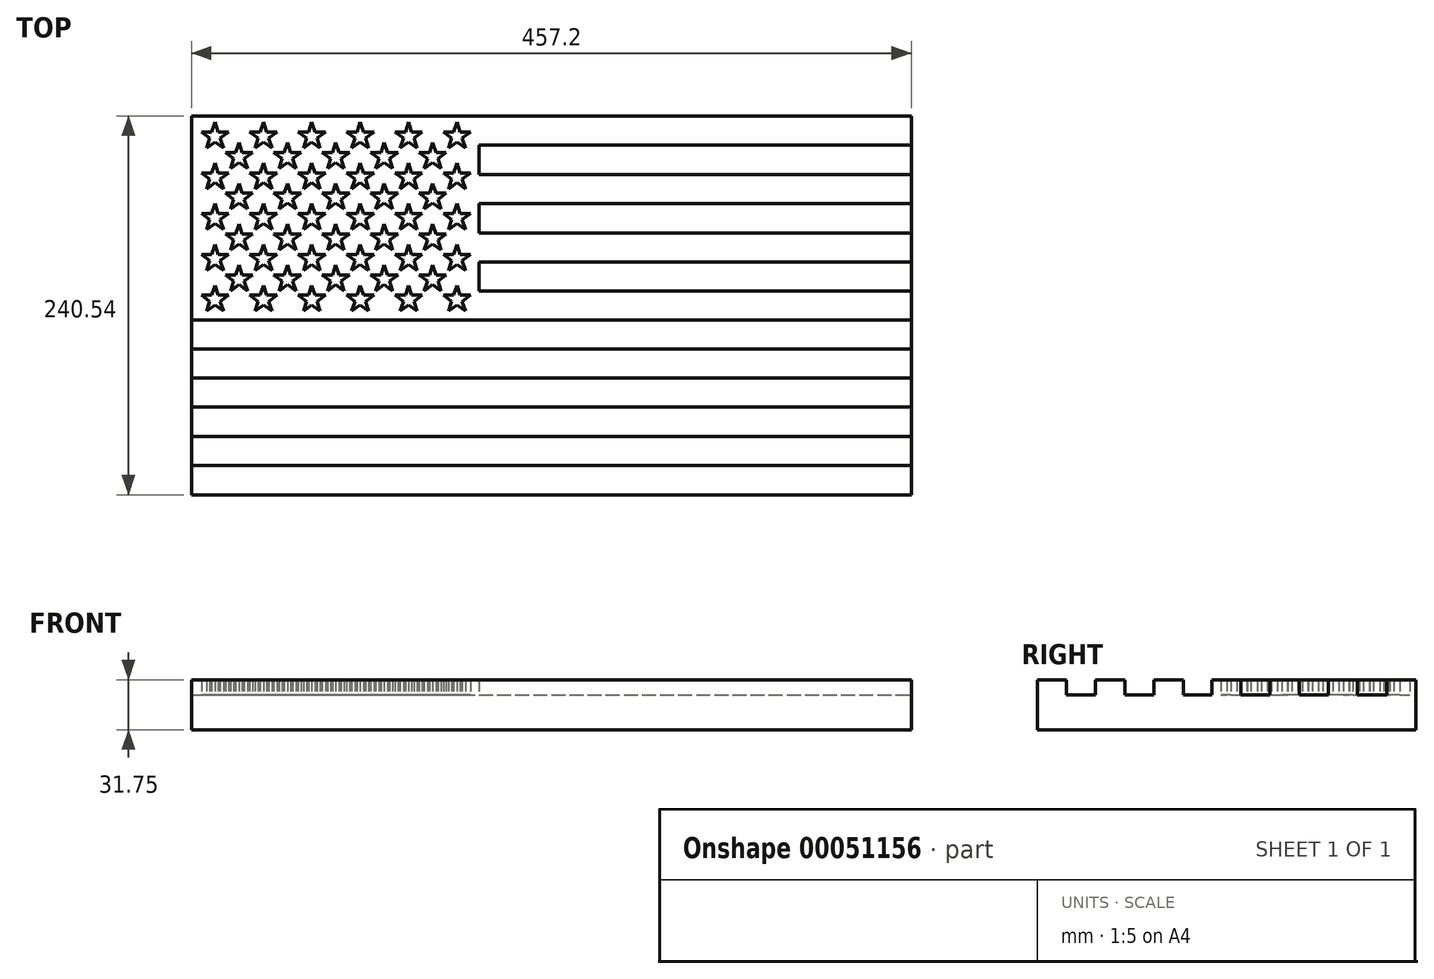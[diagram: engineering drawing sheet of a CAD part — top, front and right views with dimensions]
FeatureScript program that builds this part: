
annotation { "Feature Type Name" : "Feature", "Feature Type Description" : "" }
export const myFeature = defineFeature(function(context is Context, id is Id, definition is map)
    precondition{}
    {
        {
            var Q0;
            Q0=qCreatedBy(makeId("Top.planeOp"),FACE);
            var sketch = newSketch(context, id + "F0", { "sketchPlane" : qUnion([Q0])});
            skLineSegment(sketch, "E0.rect.bottom", {"start": v(228.6, 120.27) * mm, "end": v(-228.6, 120.27) * mm});
            skLineSegment(sketch, "E0.rect.top", {"start": v(228.6, -120.27) * mm, "end": v(-228.6, -120.27) * mm});
            skLineSegment(sketch, "E0.rect.left", {"start": v(228.6, 120.27) * mm, "end": v(228.6, -120.27) * mm});
            skLineSegment(sketch, "E0.rect.right", {"start": v(-228.6, 120.27) * mm, "end": v(-228.6, -120.27) * mm});
            skPoint(sketch, "E0.rect.middle", {"position": v(0, 0) * mm});
            skSolve(sketch);
        }
        {
            var Q0;
            Q0 = qSketchRegion(id + "F0", true);
            extrude(context, id + "F1", {"entities" : qUnion([Q0]), "depth" : 22.22 * mm});
        }
        {
            var Q0;
            Q0=makeQuery(id+"F1.opExtrude","CAP_FACE",FACE,{"disambiguationData":[OSD([sQuery(id+"F0.wireOp",EDGE,"E0.rect.bottom"),sQuery(id+"F0.wireOp",EDGE,"E0.rect.top"),sQuery(id+"F0.wireOp",EDGE,"E0.rect.left"),sQuery(id+"F0.wireOp",EDGE,"E0.rect.right")])],"isStart":false});
            var sketch = newSketch(context, id + "F2", { "sketchPlane" : qUnion([Q0])});
            skLineSegment(sketch, "E1.bottom", {"start": v(-228.6, 120.27) * mm, "end": v(-45.97, 120.27) * mm});
            skLineSegment(sketch, "E1.top", {"start": v(-228.6, -9.25) * mm, "end": v(-45.97, -9.25) * mm});
            skLineSegment(sketch, "E1.left", {"start": v(-228.6, 120.27) * mm, "end": v(-228.6, -9.25) * mm});
            skLineSegment(sketch, "E1.right", {"start": v(-45.97, 120.27) * mm, "end": v(-45.97, -9.25) * mm});
            skLineSegment(sketch, "E2.bottom", {"start": v(-45.97, 120.27) * mm, "end": v(228.6, 120.27) * mm});
            skLineSegment(sketch, "E2.top", {"start": v(-45.97, 101.73) * mm, "end": v(228.6, 101.73) * mm});
            skLineSegment(sketch, "E2.left", {"start": v(-45.97, 120.27) * mm, "end": v(-45.97, 101.73) * mm});
            skLineSegment(sketch, "E2.right", {"start": v(228.6, 120.27) * mm, "end": v(228.6, 101.73) * mm});
            skLineSegment(sketch, "E3.MirrorCS", {"start": v(-45.97, 83.19) * mm, "end": v(228.6, 83.19) * mm});
            skLineSegment(sketch, "E4.MirrorCS", {"start": v(-45.97, 64.64) * mm, "end": v(228.6, 64.64) * mm});
            skLineSegment(sketch, "E5.MirrorCS", {"start": v(-45.97, 46.1) * mm, "end": v(228.6, 46.1) * mm});
            skLineSegment(sketch, "E6.MirrorCS", {"start": v(-45.97, 27.56) * mm, "end": v(228.6, 27.56) * mm});
            skLineSegment(sketch, "E7.MirrorCS", {"start": v(-45.97, 9.02) * mm, "end": v(228.6, 9.02) * mm});
            skLineSegment(sketch, "E8", {"start": v(-45.97, -9.25) * mm, "end": v(228.6, -9.25) * mm});
            skLineSegment(sketch, "E9.bottom", {"start": v(-228.6, -120.27) * mm, "end": v(228.6, -120.27) * mm});
            skLineSegment(sketch, "E9.top", {"start": v(-228.6, -101.73) * mm, "end": v(228.6, -101.73) * mm});
            skLineSegment(sketch, "E9.left", {"start": v(-228.6, -120.27) * mm, "end": v(-228.6, -101.73) * mm});
            skLineSegment(sketch, "E9.right", {"start": v(228.6, -120.27) * mm, "end": v(228.6, -101.73) * mm});
            skLineSegment(sketch, "E10.MirrorCS", {"start": v(-228.6, -83.19) * mm, "end": v(228.6, -83.19) * mm});
            skLineSegment(sketch, "E11.MirrorCS", {"start": v(-228.6, -64.64) * mm, "end": v(228.6, -64.64) * mm});
            skLineSegment(sketch, "E12.MirrorCS", {"start": v(-228.6, -46.1) * mm, "end": v(228.6, -46.1) * mm});
            skLineSegment(sketch, "E13.MirrorCS", {"start": v(-228.6, -27.56) * mm, "end": v(228.6, -27.56) * mm});
            skLineSegment(sketch, "E14.bottom", {"start": v(-228.6, 120.27) * mm, "end": v(-213.61, 120.27) * mm});
            skLineSegment(sketch, "E14.left", {"start": v(-228.6, 120.27) * mm, "end": v(-228.6, 107.31) * mm});
            skLineSegment(sketch, "E15.trimOffspring", {"start": v(-210.03, 108.18) * mm, "end": v(-210.03, 108.18) * mm});
            skLineSegment(sketch, "E16", {"start": v(-222.27, 110.13) * mm, "end": v(-215.66, 110.13) * mm});
            skLineSegment(sketch, "E17", {"start": v(-204.95, 110.13) * mm, "end": v(-210.3, 106.24) * mm});
            skLineSegment(sketch, "E18", {"start": v(-218.97, 99.95) * mm, "end": v(-216.92, 106.24) * mm});
            skLineSegment(sketch, "E19", {"start": v(-213.61, 116.42) * mm, "end": v(-211.57, 110.13) * mm});
            skLineSegment(sketch, "E20", {"start": v(-208.26, 99.95) * mm, "end": v(-213.61, 103.84) * mm});
            skLineSegment(sketch, "E21.trimOffspring", {"start": v(-210.3, 106.24) * mm, "end": v(-208.26, 99.95) * mm});
            skLineSegment(sketch, "E22.trimOffspring", {"start": v(-211.57, 110.13) * mm, "end": v(-204.95, 110.13) * mm});
            skLineSegment(sketch, "E23.trimOffspring", {"start": v(-215.66, 110.13) * mm, "end": v(-213.61, 116.42) * mm});
            skLineSegment(sketch, "E24.trimOffspring", {"start": v(-216.92, 106.24) * mm, "end": v(-222.27, 110.13) * mm});
            skLineSegment(sketch, "E25.trimOffspring", {"start": v(-213.61, 103.84) * mm, "end": v(-218.97, 99.95) * mm});
            skLineSegment(sketch, "E26.0.1.0", {"start": v(-218.97, 74.04) * mm, "end": v(-216.92, 80.33) * mm});
            skLineSegment(sketch, "E26.0.1.1", {"start": v(-210.3, 80.33) * mm, "end": v(-208.26, 74.04) * mm});
            skLineSegment(sketch, "E26.0.1.2", {"start": v(-211.57, 84.22) * mm, "end": v(-204.95, 84.22) * mm});
            skLineSegment(sketch, "E26.0.1.3", {"start": v(-216.92, 80.33) * mm, "end": v(-222.27, 84.22) * mm});
            skLineSegment(sketch, "E26.0.1.4", {"start": v(-213.61, 77.93) * mm, "end": v(-218.97, 74.04) * mm});
            skLineSegment(sketch, "E26.0.1.5", {"start": v(-213.61, 90.51) * mm, "end": v(-211.57, 84.22) * mm});
            skLineSegment(sketch, "E26.0.1.6", {"start": v(-215.66, 84.22) * mm, "end": v(-213.61, 90.51) * mm});
            skLineSegment(sketch, "E26.0.1.7", {"start": v(-222.27, 84.22) * mm, "end": v(-215.66, 84.22) * mm});
            skLineSegment(sketch, "E26.0.1.8", {"start": v(-208.26, 74.04) * mm, "end": v(-213.61, 77.93) * mm});
            skLineSegment(sketch, "E26.0.1.9", {"start": v(-204.95, 84.22) * mm, "end": v(-210.3, 80.33) * mm});
            skLineSegment(sketch, "E26.0.2.0", {"start": v(-218.97, 48.13) * mm, "end": v(-216.92, 54.42) * mm});
            skLineSegment(sketch, "E26.0.2.1", {"start": v(-210.3, 54.42) * mm, "end": v(-208.26, 48.13) * mm});
            skLineSegment(sketch, "E26.0.2.2", {"start": v(-211.57, 58.31) * mm, "end": v(-204.95, 58.31) * mm});
            skLineSegment(sketch, "E26.0.2.3", {"start": v(-216.92, 54.42) * mm, "end": v(-222.27, 58.31) * mm});
            skLineSegment(sketch, "E26.0.2.4", {"start": v(-213.61, 52.02) * mm, "end": v(-218.97, 48.13) * mm});
            skLineSegment(sketch, "E26.0.2.5", {"start": v(-213.61, 64.6) * mm, "end": v(-211.57, 58.31) * mm});
            skLineSegment(sketch, "E26.0.2.6", {"start": v(-215.66, 58.31) * mm, "end": v(-213.61, 64.6) * mm});
            skLineSegment(sketch, "E26.0.2.7", {"start": v(-222.27, 58.31) * mm, "end": v(-215.66, 58.31) * mm});
            skLineSegment(sketch, "E26.0.2.8", {"start": v(-208.26, 48.13) * mm, "end": v(-213.61, 52.02) * mm});
            skLineSegment(sketch, "E26.0.2.9", {"start": v(-204.95, 58.31) * mm, "end": v(-210.3, 54.42) * mm});
            skLineSegment(sketch, "E26.0.3.0", {"start": v(-218.97, 22.23) * mm, "end": v(-216.92, 28.52) * mm});
            skLineSegment(sketch, "E26.0.3.1", {"start": v(-210.3, 28.52) * mm, "end": v(-208.26, 22.23) * mm});
            skLineSegment(sketch, "E26.0.3.2", {"start": v(-211.57, 32.4) * mm, "end": v(-204.95, 32.4) * mm});
            skLineSegment(sketch, "E26.0.3.3", {"start": v(-216.92, 28.52) * mm, "end": v(-222.27, 32.4) * mm});
            skLineSegment(sketch, "E26.0.3.4", {"start": v(-213.61, 26.11) * mm, "end": v(-218.97, 22.23) * mm});
            skLineSegment(sketch, "E26.0.3.5", {"start": v(-213.61, 38.7) * mm, "end": v(-211.57, 32.4) * mm});
            skLineSegment(sketch, "E26.0.3.6", {"start": v(-215.66, 32.4) * mm, "end": v(-213.61, 38.7) * mm});
            skLineSegment(sketch, "E26.0.3.7", {"start": v(-222.27, 32.4) * mm, "end": v(-215.66, 32.4) * mm});
            skLineSegment(sketch, "E26.0.3.8", {"start": v(-208.26, 22.23) * mm, "end": v(-213.61, 26.11) * mm});
            skLineSegment(sketch, "E26.0.3.9", {"start": v(-204.95, 32.4) * mm, "end": v(-210.3, 28.52) * mm});
            skLineSegment(sketch, "E26.0.4.0", {"start": v(-218.97, -3.68) * mm, "end": v(-216.92, 2.6) * mm});
            skLineSegment(sketch, "E26.0.4.1", {"start": v(-210.3, 2.6) * mm, "end": v(-208.26, -3.68) * mm});
            skLineSegment(sketch, "E26.0.4.2", {"start": v(-211.57, 6.5) * mm, "end": v(-204.95, 6.5) * mm});
            skLineSegment(sketch, "E26.0.4.3", {"start": v(-216.92, 2.6) * mm, "end": v(-222.27, 6.5) * mm});
            skLineSegment(sketch, "E26.0.4.4", {"start": v(-213.61, 0.2) * mm, "end": v(-218.97, -3.68) * mm});
            skLineSegment(sketch, "E26.0.4.5", {"start": v(-213.61, 12.79) * mm, "end": v(-211.57, 6.5) * mm});
            skLineSegment(sketch, "E26.0.4.6", {"start": v(-215.66, 6.5) * mm, "end": v(-213.61, 12.79) * mm});
            skLineSegment(sketch, "E26.0.4.7", {"start": v(-222.27, 6.5) * mm, "end": v(-215.66, 6.5) * mm});
            skLineSegment(sketch, "E26.0.4.8", {"start": v(-208.26, -3.68) * mm, "end": v(-213.61, 0.2) * mm});
            skLineSegment(sketch, "E26.0.4.9", {"start": v(-204.95, 6.5) * mm, "end": v(-210.3, 2.6) * mm});
            skLineSegment(sketch, "E26.1.0.0", {"start": v(-188.23, 99.95) * mm, "end": v(-186.19, 106.24) * mm});
            skLineSegment(sketch, "E26.1.0.1", {"start": v(-179.57, 106.24) * mm, "end": v(-177.53, 99.95) * mm});
            skLineSegment(sketch, "E26.1.0.2", {"start": v(-180.84, 110.13) * mm, "end": v(-174.22, 110.13) * mm});
            skLineSegment(sketch, "E26.1.0.3", {"start": v(-186.19, 106.24) * mm, "end": v(-191.54, 110.13) * mm});
            skLineSegment(sketch, "E26.1.0.4", {"start": v(-182.88, 103.84) * mm, "end": v(-188.23, 99.95) * mm});
            skLineSegment(sketch, "E26.1.0.5", {"start": v(-182.88, 116.42) * mm, "end": v(-180.84, 110.13) * mm});
            skLineSegment(sketch, "E26.1.0.6", {"start": v(-184.92, 110.13) * mm, "end": v(-182.88, 116.42) * mm});
            skLineSegment(sketch, "E26.1.0.7", {"start": v(-191.54, 110.13) * mm, "end": v(-184.92, 110.13) * mm});
            skLineSegment(sketch, "E26.1.0.8", {"start": v(-177.53, 99.95) * mm, "end": v(-182.88, 103.84) * mm});
            skLineSegment(sketch, "E26.1.0.9", {"start": v(-174.22, 110.13) * mm, "end": v(-179.57, 106.24) * mm});
            skLineSegment(sketch, "E26.1.1.0", {"start": v(-188.23, 74.04) * mm, "end": v(-186.19, 80.33) * mm});
            skLineSegment(sketch, "E26.1.1.1", {"start": v(-179.57, 80.33) * mm, "end": v(-177.53, 74.04) * mm});
            skLineSegment(sketch, "E26.1.1.2", {"start": v(-180.84, 84.22) * mm, "end": v(-174.22, 84.22) * mm});
            skLineSegment(sketch, "E26.1.1.3", {"start": v(-186.19, 80.33) * mm, "end": v(-191.54, 84.22) * mm});
            skLineSegment(sketch, "E26.1.1.4", {"start": v(-182.88, 77.93) * mm, "end": v(-188.23, 74.04) * mm});
            skLineSegment(sketch, "E26.1.1.5", {"start": v(-182.88, 90.51) * mm, "end": v(-180.84, 84.22) * mm});
            skLineSegment(sketch, "E26.1.1.6", {"start": v(-184.92, 84.22) * mm, "end": v(-182.88, 90.51) * mm});
            skLineSegment(sketch, "E26.1.1.7", {"start": v(-191.54, 84.22) * mm, "end": v(-184.92, 84.22) * mm});
            skLineSegment(sketch, "E26.1.1.8", {"start": v(-177.53, 74.04) * mm, "end": v(-182.88, 77.93) * mm});
            skLineSegment(sketch, "E26.1.1.9", {"start": v(-174.22, 84.22) * mm, "end": v(-179.57, 80.33) * mm});
            skLineSegment(sketch, "E26.1.2.0", {"start": v(-188.23, 48.13) * mm, "end": v(-186.19, 54.42) * mm});
            skLineSegment(sketch, "E26.1.2.1", {"start": v(-179.57, 54.42) * mm, "end": v(-177.53, 48.13) * mm});
            skLineSegment(sketch, "E26.1.2.2", {"start": v(-180.84, 58.31) * mm, "end": v(-174.22, 58.31) * mm});
            skLineSegment(sketch, "E26.1.2.3", {"start": v(-186.19, 54.42) * mm, "end": v(-191.54, 58.31) * mm});
            skLineSegment(sketch, "E26.1.2.4", {"start": v(-182.88, 52.02) * mm, "end": v(-188.23, 48.13) * mm});
            skLineSegment(sketch, "E26.1.2.5", {"start": v(-182.88, 64.6) * mm, "end": v(-180.84, 58.31) * mm});
            skLineSegment(sketch, "E26.1.2.6", {"start": v(-184.92, 58.31) * mm, "end": v(-182.88, 64.6) * mm});
            skLineSegment(sketch, "E26.1.2.7", {"start": v(-191.54, 58.31) * mm, "end": v(-184.92, 58.31) * mm});
            skLineSegment(sketch, "E26.1.2.8", {"start": v(-177.53, 48.13) * mm, "end": v(-182.88, 52.02) * mm});
            skLineSegment(sketch, "E26.1.2.9", {"start": v(-174.22, 58.31) * mm, "end": v(-179.57, 54.42) * mm});
            skLineSegment(sketch, "E26.1.3.0", {"start": v(-188.23, 22.23) * mm, "end": v(-186.19, 28.52) * mm});
            skLineSegment(sketch, "E26.1.3.1", {"start": v(-179.57, 28.52) * mm, "end": v(-177.53, 22.23) * mm});
            skLineSegment(sketch, "E26.1.3.2", {"start": v(-180.84, 32.4) * mm, "end": v(-174.22, 32.4) * mm});
            skLineSegment(sketch, "E26.1.3.3", {"start": v(-186.19, 28.52) * mm, "end": v(-191.54, 32.4) * mm});
            skLineSegment(sketch, "E26.1.3.4", {"start": v(-182.88, 26.11) * mm, "end": v(-188.23, 22.23) * mm});
            skLineSegment(sketch, "E26.1.3.5", {"start": v(-182.88, 38.7) * mm, "end": v(-180.84, 32.4) * mm});
            skLineSegment(sketch, "E26.1.3.6", {"start": v(-184.92, 32.4) * mm, "end": v(-182.88, 38.7) * mm});
            skLineSegment(sketch, "E26.1.3.7", {"start": v(-191.54, 32.4) * mm, "end": v(-184.92, 32.4) * mm});
            skLineSegment(sketch, "E26.1.3.8", {"start": v(-177.53, 22.23) * mm, "end": v(-182.88, 26.11) * mm});
            skLineSegment(sketch, "E26.1.3.9", {"start": v(-174.22, 32.4) * mm, "end": v(-179.57, 28.52) * mm});
            skLineSegment(sketch, "E26.1.4.0", {"start": v(-188.23, -3.68) * mm, "end": v(-186.19, 2.6) * mm});
            skLineSegment(sketch, "E26.1.4.1", {"start": v(-179.57, 2.6) * mm, "end": v(-177.53, -3.68) * mm});
            skLineSegment(sketch, "E26.1.4.2", {"start": v(-180.84, 6.5) * mm, "end": v(-174.22, 6.5) * mm});
            skLineSegment(sketch, "E26.1.4.3", {"start": v(-186.19, 2.6) * mm, "end": v(-191.54, 6.5) * mm});
            skLineSegment(sketch, "E26.1.4.4", {"start": v(-182.88, 0.2) * mm, "end": v(-188.23, -3.68) * mm});
            skLineSegment(sketch, "E26.1.4.5", {"start": v(-182.88, 12.79) * mm, "end": v(-180.84, 6.5) * mm});
            skLineSegment(sketch, "E26.1.4.6", {"start": v(-184.92, 6.5) * mm, "end": v(-182.88, 12.79) * mm});
            skLineSegment(sketch, "E26.1.4.7", {"start": v(-191.54, 6.5) * mm, "end": v(-184.92, 6.5) * mm});
            skLineSegment(sketch, "E26.1.4.8", {"start": v(-177.53, -3.68) * mm, "end": v(-182.88, 0.2) * mm});
            skLineSegment(sketch, "E26.1.4.9", {"start": v(-174.22, 6.5) * mm, "end": v(-179.57, 2.6) * mm});
            skLineSegment(sketch, "E26.2.0.0", {"start": v(-157.5, 99.95) * mm, "end": v(-155.45, 106.24) * mm});
            skLineSegment(sketch, "E26.2.0.1", {"start": v(-148.84, 106.24) * mm, "end": v(-146.8, 99.95) * mm});
            skLineSegment(sketch, "E26.2.0.2", {"start": v(-150.1, 110.13) * mm, "end": v(-143.49, 110.13) * mm});
            skLineSegment(sketch, "E26.2.0.3", {"start": v(-155.45, 106.24) * mm, "end": v(-160.8, 110.13) * mm});
            skLineSegment(sketch, "E26.2.0.4", {"start": v(-152.15, 103.84) * mm, "end": v(-157.5, 99.95) * mm});
            skLineSegment(sketch, "E26.2.0.5", {"start": v(-152.15, 116.42) * mm, "end": v(-150.1, 110.13) * mm});
            skLineSegment(sketch, "E26.2.0.6", {"start": v(-154.2, 110.13) * mm, "end": v(-152.15, 116.42) * mm});
            skLineSegment(sketch, "E26.2.0.7", {"start": v(-160.8, 110.13) * mm, "end": v(-154.2, 110.13) * mm});
            skLineSegment(sketch, "E26.2.0.8", {"start": v(-146.8, 99.95) * mm, "end": v(-152.15, 103.84) * mm});
            skLineSegment(sketch, "E26.2.0.9", {"start": v(-143.49, 110.13) * mm, "end": v(-148.84, 106.24) * mm});
            skLineSegment(sketch, "E26.2.1.0", {"start": v(-157.5, 74.04) * mm, "end": v(-155.45, 80.33) * mm});
            skLineSegment(sketch, "E26.2.1.1", {"start": v(-148.84, 80.33) * mm, "end": v(-146.8, 74.04) * mm});
            skLineSegment(sketch, "E26.2.1.2", {"start": v(-150.1, 84.22) * mm, "end": v(-143.49, 84.22) * mm});
            skLineSegment(sketch, "E26.2.1.3", {"start": v(-155.45, 80.33) * mm, "end": v(-160.8, 84.22) * mm});
            skLineSegment(sketch, "E26.2.1.4", {"start": v(-152.15, 77.93) * mm, "end": v(-157.5, 74.04) * mm});
            skLineSegment(sketch, "E26.2.1.5", {"start": v(-152.15, 90.51) * mm, "end": v(-150.1, 84.22) * mm});
            skLineSegment(sketch, "E26.2.1.6", {"start": v(-154.2, 84.22) * mm, "end": v(-152.15, 90.51) * mm});
            skLineSegment(sketch, "E26.2.1.7", {"start": v(-160.8, 84.22) * mm, "end": v(-154.2, 84.22) * mm});
            skLineSegment(sketch, "E26.2.1.8", {"start": v(-146.8, 74.04) * mm, "end": v(-152.15, 77.93) * mm});
            skLineSegment(sketch, "E26.2.1.9", {"start": v(-143.49, 84.22) * mm, "end": v(-148.84, 80.33) * mm});
            skLineSegment(sketch, "E26.2.2.0", {"start": v(-157.5, 48.13) * mm, "end": v(-155.45, 54.42) * mm});
            skLineSegment(sketch, "E26.2.2.1", {"start": v(-148.84, 54.42) * mm, "end": v(-146.8, 48.13) * mm});
            skLineSegment(sketch, "E26.2.2.2", {"start": v(-150.1, 58.31) * mm, "end": v(-143.49, 58.31) * mm});
            skLineSegment(sketch, "E26.2.2.3", {"start": v(-155.45, 54.42) * mm, "end": v(-160.8, 58.31) * mm});
            skLineSegment(sketch, "E26.2.2.4", {"start": v(-152.15, 52.02) * mm, "end": v(-157.5, 48.13) * mm});
            skLineSegment(sketch, "E26.2.2.5", {"start": v(-152.15, 64.6) * mm, "end": v(-150.1, 58.31) * mm});
            skLineSegment(sketch, "E26.2.2.6", {"start": v(-154.2, 58.31) * mm, "end": v(-152.15, 64.6) * mm});
            skLineSegment(sketch, "E26.2.2.7", {"start": v(-160.8, 58.31) * mm, "end": v(-154.2, 58.31) * mm});
            skLineSegment(sketch, "E26.2.2.8", {"start": v(-146.8, 48.13) * mm, "end": v(-152.15, 52.02) * mm});
            skLineSegment(sketch, "E26.2.2.9", {"start": v(-143.49, 58.31) * mm, "end": v(-148.84, 54.42) * mm});
            skLineSegment(sketch, "E26.2.3.0", {"start": v(-157.5, 22.23) * mm, "end": v(-155.45, 28.52) * mm});
            skLineSegment(sketch, "E26.2.3.1", {"start": v(-148.84, 28.52) * mm, "end": v(-146.8, 22.23) * mm});
            skLineSegment(sketch, "E26.2.3.2", {"start": v(-150.1, 32.4) * mm, "end": v(-143.49, 32.4) * mm});
            skLineSegment(sketch, "E26.2.3.3", {"start": v(-155.45, 28.52) * mm, "end": v(-160.8, 32.4) * mm});
            skLineSegment(sketch, "E26.2.3.4", {"start": v(-152.15, 26.11) * mm, "end": v(-157.5, 22.23) * mm});
            skLineSegment(sketch, "E26.2.3.5", {"start": v(-152.15, 38.7) * mm, "end": v(-150.1, 32.4) * mm});
            skLineSegment(sketch, "E26.2.3.6", {"start": v(-154.2, 32.4) * mm, "end": v(-152.15, 38.7) * mm});
            skLineSegment(sketch, "E26.2.3.7", {"start": v(-160.8, 32.4) * mm, "end": v(-154.2, 32.4) * mm});
            skLineSegment(sketch, "E26.2.3.8", {"start": v(-146.8, 22.23) * mm, "end": v(-152.15, 26.11) * mm});
            skLineSegment(sketch, "E26.2.3.9", {"start": v(-143.49, 32.4) * mm, "end": v(-148.84, 28.52) * mm});
            skLineSegment(sketch, "E26.2.4.0", {"start": v(-157.5, -3.68) * mm, "end": v(-155.45, 2.6) * mm});
            skLineSegment(sketch, "E26.2.4.1", {"start": v(-148.84, 2.6) * mm, "end": v(-146.8, -3.68) * mm});
            skLineSegment(sketch, "E26.2.4.2", {"start": v(-150.1, 6.5) * mm, "end": v(-143.49, 6.5) * mm});
            skLineSegment(sketch, "E26.2.4.3", {"start": v(-155.45, 2.6) * mm, "end": v(-160.8, 6.5) * mm});
            skLineSegment(sketch, "E26.2.4.4", {"start": v(-152.15, 0.2) * mm, "end": v(-157.5, -3.68) * mm});
            skLineSegment(sketch, "E26.2.4.5", {"start": v(-152.15, 12.79) * mm, "end": v(-150.1, 6.5) * mm});
            skLineSegment(sketch, "E26.2.4.6", {"start": v(-154.2, 6.5) * mm, "end": v(-152.15, 12.79) * mm});
            skLineSegment(sketch, "E26.2.4.7", {"start": v(-160.8, 6.5) * mm, "end": v(-154.2, 6.5) * mm});
            skLineSegment(sketch, "E26.2.4.8", {"start": v(-146.8, -3.68) * mm, "end": v(-152.15, 0.2) * mm});
            skLineSegment(sketch, "E26.2.4.9", {"start": v(-143.49, 6.5) * mm, "end": v(-148.84, 2.6) * mm});
            skLineSegment(sketch, "E26.3.0.0", {"start": v(-126.76, 99.95) * mm, "end": v(-124.72, 106.24) * mm});
            skLineSegment(sketch, "E26.3.0.1", {"start": v(-118.1, 106.24) * mm, "end": v(-116.06, 99.95) * mm});
            skLineSegment(sketch, "E26.3.0.2", {"start": v(-119.37, 110.13) * mm, "end": v(-112.75, 110.13) * mm});
            skLineSegment(sketch, "E26.3.0.3", {"start": v(-124.72, 106.24) * mm, "end": v(-130.07, 110.13) * mm});
            skLineSegment(sketch, "E26.3.0.4", {"start": v(-121.41, 103.84) * mm, "end": v(-126.76, 99.95) * mm});
            skLineSegment(sketch, "E26.3.0.5", {"start": v(-121.41, 116.42) * mm, "end": v(-119.37, 110.13) * mm});
            skLineSegment(sketch, "E26.3.0.6", {"start": v(-123.46, 110.13) * mm, "end": v(-121.41, 116.42) * mm});
            skLineSegment(sketch, "E26.3.0.7", {"start": v(-130.07, 110.13) * mm, "end": v(-123.46, 110.13) * mm});
            skLineSegment(sketch, "E26.3.0.8", {"start": v(-116.06, 99.95) * mm, "end": v(-121.41, 103.84) * mm});
            skLineSegment(sketch, "E26.3.0.9", {"start": v(-112.75, 110.13) * mm, "end": v(-118.1, 106.24) * mm});
            skLineSegment(sketch, "E26.3.1.0", {"start": v(-126.76, 74.04) * mm, "end": v(-124.72, 80.33) * mm});
            skLineSegment(sketch, "E26.3.1.1", {"start": v(-118.1, 80.33) * mm, "end": v(-116.06, 74.04) * mm});
            skLineSegment(sketch, "E26.3.1.2", {"start": v(-119.37, 84.22) * mm, "end": v(-112.75, 84.22) * mm});
            skLineSegment(sketch, "E26.3.1.3", {"start": v(-124.72, 80.33) * mm, "end": v(-130.07, 84.22) * mm});
            skLineSegment(sketch, "E26.3.1.4", {"start": v(-121.41, 77.93) * mm, "end": v(-126.76, 74.04) * mm});
            skLineSegment(sketch, "E26.3.1.5", {"start": v(-121.41, 90.51) * mm, "end": v(-119.37, 84.22) * mm});
            skLineSegment(sketch, "E26.3.1.6", {"start": v(-123.46, 84.22) * mm, "end": v(-121.41, 90.51) * mm});
            skLineSegment(sketch, "E26.3.1.7", {"start": v(-130.07, 84.22) * mm, "end": v(-123.46, 84.22) * mm});
            skLineSegment(sketch, "E26.3.1.8", {"start": v(-116.06, 74.04) * mm, "end": v(-121.41, 77.93) * mm});
            skLineSegment(sketch, "E26.3.1.9", {"start": v(-112.75, 84.22) * mm, "end": v(-118.1, 80.33) * mm});
            skLineSegment(sketch, "E26.3.2.0", {"start": v(-126.76, 48.13) * mm, "end": v(-124.72, 54.42) * mm});
            skLineSegment(sketch, "E26.3.2.1", {"start": v(-118.1, 54.42) * mm, "end": v(-116.06, 48.13) * mm});
            skLineSegment(sketch, "E26.3.2.2", {"start": v(-119.37, 58.31) * mm, "end": v(-112.75, 58.31) * mm});
            skLineSegment(sketch, "E26.3.2.3", {"start": v(-124.72, 54.42) * mm, "end": v(-130.07, 58.31) * mm});
            skLineSegment(sketch, "E26.3.2.4", {"start": v(-121.41, 52.02) * mm, "end": v(-126.76, 48.13) * mm});
            skLineSegment(sketch, "E26.3.2.5", {"start": v(-121.41, 64.6) * mm, "end": v(-119.37, 58.31) * mm});
            skLineSegment(sketch, "E26.3.2.6", {"start": v(-123.46, 58.31) * mm, "end": v(-121.41, 64.6) * mm});
            skLineSegment(sketch, "E26.3.2.7", {"start": v(-130.07, 58.31) * mm, "end": v(-123.46, 58.31) * mm});
            skLineSegment(sketch, "E26.3.2.8", {"start": v(-116.06, 48.13) * mm, "end": v(-121.41, 52.02) * mm});
            skLineSegment(sketch, "E26.3.2.9", {"start": v(-112.75, 58.31) * mm, "end": v(-118.1, 54.42) * mm});
            skLineSegment(sketch, "E26.3.3.0", {"start": v(-126.76, 22.23) * mm, "end": v(-124.72, 28.52) * mm});
            skLineSegment(sketch, "E26.3.3.1", {"start": v(-118.1, 28.52) * mm, "end": v(-116.06, 22.23) * mm});
            skLineSegment(sketch, "E26.3.3.2", {"start": v(-119.37, 32.4) * mm, "end": v(-112.75, 32.4) * mm});
            skLineSegment(sketch, "E26.3.3.3", {"start": v(-124.72, 28.52) * mm, "end": v(-130.07, 32.4) * mm});
            skLineSegment(sketch, "E26.3.3.4", {"start": v(-121.41, 26.11) * mm, "end": v(-126.76, 22.23) * mm});
            skLineSegment(sketch, "E26.3.3.5", {"start": v(-121.41, 38.7) * mm, "end": v(-119.37, 32.4) * mm});
            skLineSegment(sketch, "E26.3.3.6", {"start": v(-123.46, 32.4) * mm, "end": v(-121.41, 38.7) * mm});
            skLineSegment(sketch, "E26.3.3.7", {"start": v(-130.07, 32.4) * mm, "end": v(-123.46, 32.4) * mm});
            skLineSegment(sketch, "E26.3.3.8", {"start": v(-116.06, 22.23) * mm, "end": v(-121.41, 26.11) * mm});
            skLineSegment(sketch, "E26.3.3.9", {"start": v(-112.75, 32.4) * mm, "end": v(-118.1, 28.52) * mm});
            skLineSegment(sketch, "E26.3.4.0", {"start": v(-126.76, -3.68) * mm, "end": v(-124.72, 2.6) * mm});
            skLineSegment(sketch, "E26.3.4.1", {"start": v(-118.1, 2.6) * mm, "end": v(-116.06, -3.68) * mm});
            skLineSegment(sketch, "E26.3.4.2", {"start": v(-119.37, 6.5) * mm, "end": v(-112.75, 6.5) * mm});
            skLineSegment(sketch, "E26.3.4.3", {"start": v(-124.72, 2.6) * mm, "end": v(-130.07, 6.5) * mm});
            skLineSegment(sketch, "E26.3.4.4", {"start": v(-121.41, 0.2) * mm, "end": v(-126.76, -3.68) * mm});
            skLineSegment(sketch, "E26.3.4.5", {"start": v(-121.41, 12.79) * mm, "end": v(-119.37, 6.5) * mm});
            skLineSegment(sketch, "E26.3.4.6", {"start": v(-123.46, 6.5) * mm, "end": v(-121.41, 12.79) * mm});
            skLineSegment(sketch, "E26.3.4.7", {"start": v(-130.07, 6.5) * mm, "end": v(-123.46, 6.5) * mm});
            skLineSegment(sketch, "E26.3.4.8", {"start": v(-116.06, -3.68) * mm, "end": v(-121.41, 0.2) * mm});
            skLineSegment(sketch, "E26.3.4.9", {"start": v(-112.75, 6.5) * mm, "end": v(-118.1, 2.6) * mm});
            skLineSegment(sketch, "E26.4.0.0", {"start": v(-96.03, 99.95) * mm, "end": v(-93.99, 106.24) * mm});
            skLineSegment(sketch, "E26.4.0.1", {"start": v(-87.37, 106.24) * mm, "end": v(-85.33, 99.95) * mm});
            skLineSegment(sketch, "E26.4.0.2", {"start": v(-88.63, 110.13) * mm, "end": v(-82.02, 110.13) * mm});
            skLineSegment(sketch, "E26.4.0.3", {"start": v(-93.99, 106.24) * mm, "end": v(-99.34, 110.13) * mm});
            skLineSegment(sketch, "E26.4.0.4", {"start": v(-90.68, 103.84) * mm, "end": v(-96.03, 99.95) * mm});
            skLineSegment(sketch, "E26.4.0.5", {"start": v(-90.68, 116.42) * mm, "end": v(-88.63, 110.13) * mm});
            skLineSegment(sketch, "E26.4.0.6", {"start": v(-92.72, 110.13) * mm, "end": v(-90.68, 116.42) * mm});
            skLineSegment(sketch, "E26.4.0.7", {"start": v(-99.34, 110.13) * mm, "end": v(-92.72, 110.13) * mm});
            skLineSegment(sketch, "E26.4.0.8", {"start": v(-85.33, 99.95) * mm, "end": v(-90.68, 103.84) * mm});
            skLineSegment(sketch, "E26.4.0.9", {"start": v(-82.02, 110.13) * mm, "end": v(-87.37, 106.24) * mm});
            skLineSegment(sketch, "E26.4.1.0", {"start": v(-96.03, 74.04) * mm, "end": v(-93.99, 80.33) * mm});
            skLineSegment(sketch, "E26.4.1.1", {"start": v(-87.37, 80.33) * mm, "end": v(-85.33, 74.04) * mm});
            skLineSegment(sketch, "E26.4.1.2", {"start": v(-88.63, 84.22) * mm, "end": v(-82.02, 84.22) * mm});
            skLineSegment(sketch, "E26.4.1.3", {"start": v(-93.99, 80.33) * mm, "end": v(-99.34, 84.22) * mm});
            skLineSegment(sketch, "E26.4.1.4", {"start": v(-90.68, 77.93) * mm, "end": v(-96.03, 74.04) * mm});
            skLineSegment(sketch, "E26.4.1.5", {"start": v(-90.68, 90.51) * mm, "end": v(-88.63, 84.22) * mm});
            skLineSegment(sketch, "E26.4.1.6", {"start": v(-92.72, 84.22) * mm, "end": v(-90.68, 90.51) * mm});
            skLineSegment(sketch, "E26.4.1.7", {"start": v(-99.34, 84.22) * mm, "end": v(-92.72, 84.22) * mm});
            skLineSegment(sketch, "E26.4.1.8", {"start": v(-85.33, 74.04) * mm, "end": v(-90.68, 77.93) * mm});
            skLineSegment(sketch, "E26.4.1.9", {"start": v(-82.02, 84.22) * mm, "end": v(-87.37, 80.33) * mm});
            skLineSegment(sketch, "E26.4.2.0", {"start": v(-96.03, 48.13) * mm, "end": v(-93.99, 54.42) * mm});
            skLineSegment(sketch, "E26.4.2.1", {"start": v(-87.37, 54.42) * mm, "end": v(-85.33, 48.13) * mm});
            skLineSegment(sketch, "E26.4.2.2", {"start": v(-88.63, 58.31) * mm, "end": v(-82.02, 58.31) * mm});
            skLineSegment(sketch, "E26.4.2.3", {"start": v(-93.99, 54.42) * mm, "end": v(-99.34, 58.31) * mm});
            skLineSegment(sketch, "E26.4.2.4", {"start": v(-90.68, 52.02) * mm, "end": v(-96.03, 48.13) * mm});
            skLineSegment(sketch, "E26.4.2.5", {"start": v(-90.68, 64.6) * mm, "end": v(-88.63, 58.31) * mm});
            skLineSegment(sketch, "E26.4.2.6", {"start": v(-92.72, 58.31) * mm, "end": v(-90.68, 64.6) * mm});
            skLineSegment(sketch, "E26.4.2.7", {"start": v(-99.34, 58.31) * mm, "end": v(-92.72, 58.31) * mm});
            skLineSegment(sketch, "E26.4.2.8", {"start": v(-85.33, 48.13) * mm, "end": v(-90.68, 52.02) * mm});
            skLineSegment(sketch, "E26.4.2.9", {"start": v(-82.02, 58.31) * mm, "end": v(-87.37, 54.42) * mm});
            skLineSegment(sketch, "E26.4.3.0", {"start": v(-96.03, 22.23) * mm, "end": v(-93.99, 28.52) * mm});
            skLineSegment(sketch, "E26.4.3.1", {"start": v(-87.37, 28.52) * mm, "end": v(-85.33, 22.23) * mm});
            skLineSegment(sketch, "E26.4.3.2", {"start": v(-88.63, 32.4) * mm, "end": v(-82.02, 32.4) * mm});
            skLineSegment(sketch, "E26.4.3.3", {"start": v(-93.99, 28.52) * mm, "end": v(-99.34, 32.4) * mm});
            skLineSegment(sketch, "E26.4.3.4", {"start": v(-90.68, 26.11) * mm, "end": v(-96.03, 22.23) * mm});
            skLineSegment(sketch, "E26.4.3.5", {"start": v(-90.68, 38.7) * mm, "end": v(-88.63, 32.4) * mm});
            skLineSegment(sketch, "E26.4.3.6", {"start": v(-92.72, 32.4) * mm, "end": v(-90.68, 38.7) * mm});
            skLineSegment(sketch, "E26.4.3.7", {"start": v(-99.34, 32.4) * mm, "end": v(-92.72, 32.4) * mm});
            skLineSegment(sketch, "E26.4.3.8", {"start": v(-85.33, 22.23) * mm, "end": v(-90.68, 26.11) * mm});
            skLineSegment(sketch, "E26.4.3.9", {"start": v(-82.02, 32.4) * mm, "end": v(-87.37, 28.52) * mm});
            skLineSegment(sketch, "E26.4.4.0", {"start": v(-96.03, -3.68) * mm, "end": v(-93.99, 2.6) * mm});
            skLineSegment(sketch, "E26.4.4.1", {"start": v(-87.37, 2.6) * mm, "end": v(-85.33, -3.68) * mm});
            skLineSegment(sketch, "E26.4.4.2", {"start": v(-88.63, 6.5) * mm, "end": v(-82.02, 6.5) * mm});
            skLineSegment(sketch, "E26.4.4.3", {"start": v(-93.99, 2.6) * mm, "end": v(-99.34, 6.5) * mm});
            skLineSegment(sketch, "E26.4.4.4", {"start": v(-90.68, 0.2) * mm, "end": v(-96.03, -3.68) * mm});
            skLineSegment(sketch, "E26.4.4.5", {"start": v(-90.68, 12.79) * mm, "end": v(-88.63, 6.5) * mm});
            skLineSegment(sketch, "E26.4.4.6", {"start": v(-92.72, 6.5) * mm, "end": v(-90.68, 12.79) * mm});
            skLineSegment(sketch, "E26.4.4.7", {"start": v(-99.34, 6.5) * mm, "end": v(-92.72, 6.5) * mm});
            skLineSegment(sketch, "E26.4.4.8", {"start": v(-85.33, -3.68) * mm, "end": v(-90.68, 0.2) * mm});
            skLineSegment(sketch, "E26.4.4.9", {"start": v(-82.02, 6.5) * mm, "end": v(-87.37, 2.6) * mm});
            skLineSegment(sketch, "E26.5.0.0", {"start": v(-65.3, 99.95) * mm, "end": v(-63.25, 106.24) * mm});
            skLineSegment(sketch, "E26.5.0.1", {"start": v(-56.64, 106.24) * mm, "end": v(-54.6, 99.95) * mm});
            skLineSegment(sketch, "E26.5.0.2", {"start": v(-57.9, 110.13) * mm, "end": v(-51.28, 110.13) * mm});
            skLineSegment(sketch, "E26.5.0.3", {"start": v(-63.25, 106.24) * mm, "end": v(-68.6, 110.13) * mm});
            skLineSegment(sketch, "E26.5.0.4", {"start": v(-59.94, 103.84) * mm, "end": v(-65.3, 99.95) * mm});
            skLineSegment(sketch, "E26.5.0.5", {"start": v(-59.94, 116.42) * mm, "end": v(-57.9, 110.13) * mm});
            skLineSegment(sketch, "E26.5.0.6", {"start": v(-61.99, 110.13) * mm, "end": v(-59.94, 116.42) * mm});
            skLineSegment(sketch, "E26.5.0.7", {"start": v(-68.6, 110.13) * mm, "end": v(-61.99, 110.13) * mm});
            skLineSegment(sketch, "E26.5.0.8", {"start": v(-54.6, 99.95) * mm, "end": v(-59.94, 103.84) * mm});
            skLineSegment(sketch, "E26.5.0.9", {"start": v(-51.28, 110.13) * mm, "end": v(-56.64, 106.24) * mm});
            skLineSegment(sketch, "E26.5.1.0", {"start": v(-65.3, 74.04) * mm, "end": v(-63.25, 80.33) * mm});
            skLineSegment(sketch, "E26.5.1.1", {"start": v(-56.64, 80.33) * mm, "end": v(-54.6, 74.04) * mm});
            skLineSegment(sketch, "E26.5.1.2", {"start": v(-57.9, 84.22) * mm, "end": v(-51.28, 84.22) * mm});
            skLineSegment(sketch, "E26.5.1.3", {"start": v(-63.25, 80.33) * mm, "end": v(-68.6, 84.22) * mm});
            skLineSegment(sketch, "E26.5.1.4", {"start": v(-59.94, 77.93) * mm, "end": v(-65.3, 74.04) * mm});
            skLineSegment(sketch, "E26.5.1.5", {"start": v(-59.94, 90.51) * mm, "end": v(-57.9, 84.22) * mm});
            skLineSegment(sketch, "E26.5.1.6", {"start": v(-61.99, 84.22) * mm, "end": v(-59.94, 90.51) * mm});
            skLineSegment(sketch, "E26.5.1.7", {"start": v(-68.6, 84.22) * mm, "end": v(-61.99, 84.22) * mm});
            skLineSegment(sketch, "E26.5.1.8", {"start": v(-54.6, 74.04) * mm, "end": v(-59.94, 77.93) * mm});
            skLineSegment(sketch, "E26.5.1.9", {"start": v(-51.28, 84.22) * mm, "end": v(-56.64, 80.33) * mm});
            skLineSegment(sketch, "E26.5.2.0", {"start": v(-65.3, 48.13) * mm, "end": v(-63.25, 54.42) * mm});
            skLineSegment(sketch, "E26.5.2.1", {"start": v(-56.64, 54.42) * mm, "end": v(-54.6, 48.13) * mm});
            skLineSegment(sketch, "E26.5.2.2", {"start": v(-57.9, 58.31) * mm, "end": v(-51.28, 58.31) * mm});
            skLineSegment(sketch, "E26.5.2.3", {"start": v(-63.25, 54.42) * mm, "end": v(-68.6, 58.31) * mm});
            skLineSegment(sketch, "E26.5.2.4", {"start": v(-59.94, 52.02) * mm, "end": v(-65.3, 48.13) * mm});
            skLineSegment(sketch, "E26.5.2.5", {"start": v(-59.94, 64.6) * mm, "end": v(-57.9, 58.31) * mm});
            skLineSegment(sketch, "E26.5.2.6", {"start": v(-61.99, 58.31) * mm, "end": v(-59.94, 64.6) * mm});
            skLineSegment(sketch, "E26.5.2.7", {"start": v(-68.6, 58.31) * mm, "end": v(-61.99, 58.31) * mm});
            skLineSegment(sketch, "E26.5.2.8", {"start": v(-54.6, 48.13) * mm, "end": v(-59.94, 52.02) * mm});
            skLineSegment(sketch, "E26.5.2.9", {"start": v(-51.28, 58.31) * mm, "end": v(-56.64, 54.42) * mm});
            skLineSegment(sketch, "E26.5.3.0", {"start": v(-65.3, 22.23) * mm, "end": v(-63.25, 28.52) * mm});
            skLineSegment(sketch, "E26.5.3.1", {"start": v(-56.64, 28.52) * mm, "end": v(-54.6, 22.23) * mm});
            skLineSegment(sketch, "E26.5.3.2", {"start": v(-57.9, 32.4) * mm, "end": v(-51.28, 32.4) * mm});
            skLineSegment(sketch, "E26.5.3.3", {"start": v(-63.25, 28.52) * mm, "end": v(-68.6, 32.4) * mm});
            skLineSegment(sketch, "E26.5.3.4", {"start": v(-59.94, 26.11) * mm, "end": v(-65.3, 22.23) * mm});
            skLineSegment(sketch, "E26.5.3.5", {"start": v(-59.94, 38.7) * mm, "end": v(-57.9, 32.4) * mm});
            skLineSegment(sketch, "E26.5.3.6", {"start": v(-61.99, 32.4) * mm, "end": v(-59.94, 38.7) * mm});
            skLineSegment(sketch, "E26.5.3.7", {"start": v(-68.6, 32.4) * mm, "end": v(-61.99, 32.4) * mm});
            skLineSegment(sketch, "E26.5.3.8", {"start": v(-54.6, 22.23) * mm, "end": v(-59.94, 26.11) * mm});
            skLineSegment(sketch, "E26.5.3.9", {"start": v(-51.28, 32.4) * mm, "end": v(-56.64, 28.52) * mm});
            skLineSegment(sketch, "E26.5.4.0", {"start": v(-65.3, -3.68) * mm, "end": v(-63.25, 2.6) * mm});
            skLineSegment(sketch, "E26.5.4.1", {"start": v(-56.64, 2.6) * mm, "end": v(-54.6, -3.68) * mm});
            skLineSegment(sketch, "E26.5.4.2", {"start": v(-57.9, 6.5) * mm, "end": v(-51.28, 6.5) * mm});
            skLineSegment(sketch, "E26.5.4.3", {"start": v(-63.25, 2.6) * mm, "end": v(-68.6, 6.5) * mm});
            skLineSegment(sketch, "E26.5.4.4", {"start": v(-59.94, 0.2) * mm, "end": v(-65.3, -3.68) * mm});
            skLineSegment(sketch, "E26.5.4.5", {"start": v(-59.94, 12.79) * mm, "end": v(-57.9, 6.5) * mm});
            skLineSegment(sketch, "E26.5.4.6", {"start": v(-61.99, 6.5) * mm, "end": v(-59.94, 12.79) * mm});
            skLineSegment(sketch, "E26.5.4.7", {"start": v(-68.6, 6.5) * mm, "end": v(-61.99, 6.5) * mm});
            skLineSegment(sketch, "E26.5.4.8", {"start": v(-54.6, -3.68) * mm, "end": v(-59.94, 0.2) * mm});
            skLineSegment(sketch, "E26.5.4.9", {"start": v(-51.28, 6.5) * mm, "end": v(-56.64, 2.6) * mm});
            skLineSegment(sketch, "E26.direction1", {"start": v(-218.97, 99.95) * mm, "end": v(-188.23, 99.95) * mm, "construction": true});
            skLineSegment(sketch, "E26.direction2", {"start": v(-218.97, 99.95) * mm, "end": v(-218.97, 74.04) * mm, "construction": true});
            skLineSegment(sketch, "E27.bottom", {"start": v(-228.6, 120.27) * mm, "end": v(-198.37, 120.27) * mm});
            skLineSegment(sketch, "E27.left", {"start": v(-228.6, 120.27) * mm, "end": v(-228.6, 94.36) * mm});
            skLineSegment(sketch, "E28", {"start": v(-198.37, 103.47) * mm, "end": v(-200.42, 97.17) * mm});
            skLineSegment(sketch, "E29", {"start": v(-203.73, 87) * mm, "end": v(-198.37, 90.88) * mm});
            skLineSegment(sketch, "E30", {"start": v(-189.71, 97.17) * mm, "end": v(-196.33, 97.17) * mm});
            skLineSegment(sketch, "E31", {"start": v(-207.03, 97.17) * mm, "end": v(-201.68, 93.29) * mm});
            skLineSegment(sketch, "E32", {"start": v(-193.02, 87) * mm, "end": v(-195.07, 93.29) * mm});
            skLineSegment(sketch, "E33.trimOffspring", {"start": v(-196.33, 97.17) * mm, "end": v(-198.37, 103.47) * mm});
            skLineSegment(sketch, "E34.trimOffspring", {"start": v(-200.42, 97.17) * mm, "end": v(-207.03, 97.17) * mm});
            skLineSegment(sketch, "E35.trimOffspring", {"start": v(-201.68, 93.29) * mm, "end": v(-203.73, 87) * mm});
            skLineSegment(sketch, "E36.trimOffspring", {"start": v(-198.37, 90.88) * mm, "end": v(-193.02, 87) * mm});
            skLineSegment(sketch, "E37.trimOffspring", {"start": v(-195.07, 93.29) * mm, "end": v(-189.71, 97.17) * mm});
            skLineSegment(sketch, "E38.0.1.0", {"start": v(-198.37, 64.98) * mm, "end": v(-193.02, 61.09) * mm});
            skLineSegment(sketch, "E38.0.1.1", {"start": v(-195.07, 67.38) * mm, "end": v(-189.71, 71.27) * mm});
            skLineSegment(sketch, "E38.0.1.2", {"start": v(-193.02, 61.09) * mm, "end": v(-195.07, 67.38) * mm});
            skLineSegment(sketch, "E38.0.1.3", {"start": v(-201.68, 67.38) * mm, "end": v(-203.73, 61.09) * mm});
            skLineSegment(sketch, "E38.0.1.4", {"start": v(-189.71, 71.27) * mm, "end": v(-196.33, 71.27) * mm});
            skLineSegment(sketch, "E38.0.1.5", {"start": v(-203.73, 61.09) * mm, "end": v(-198.37, 64.98) * mm});
            skLineSegment(sketch, "E38.0.1.6", {"start": v(-200.42, 71.27) * mm, "end": v(-207.03, 71.27) * mm});
            skLineSegment(sketch, "E38.0.1.7", {"start": v(-207.03, 71.27) * mm, "end": v(-201.68, 67.38) * mm});
            skLineSegment(sketch, "E38.0.1.8", {"start": v(-198.37, 77.56) * mm, "end": v(-200.42, 71.27) * mm});
            skLineSegment(sketch, "E38.0.1.9", {"start": v(-196.33, 71.27) * mm, "end": v(-198.37, 77.56) * mm});
            skLineSegment(sketch, "E38.0.2.0", {"start": v(-198.37, 39.07) * mm, "end": v(-193.02, 35.18) * mm});
            skLineSegment(sketch, "E38.0.2.1", {"start": v(-195.07, 41.47) * mm, "end": v(-189.71, 45.36) * mm});
            skLineSegment(sketch, "E38.0.2.2", {"start": v(-193.02, 35.18) * mm, "end": v(-195.07, 41.47) * mm});
            skLineSegment(sketch, "E38.0.2.3", {"start": v(-201.68, 41.47) * mm, "end": v(-203.73, 35.18) * mm});
            skLineSegment(sketch, "E38.0.2.4", {"start": v(-189.71, 45.36) * mm, "end": v(-196.33, 45.36) * mm});
            skLineSegment(sketch, "E38.0.2.5", {"start": v(-203.73, 35.18) * mm, "end": v(-198.37, 39.07) * mm});
            skLineSegment(sketch, "E38.0.2.6", {"start": v(-200.42, 45.36) * mm, "end": v(-207.03, 45.36) * mm});
            skLineSegment(sketch, "E38.0.2.7", {"start": v(-207.03, 45.36) * mm, "end": v(-201.68, 41.47) * mm});
            skLineSegment(sketch, "E38.0.2.8", {"start": v(-198.37, 51.65) * mm, "end": v(-200.42, 45.36) * mm});
            skLineSegment(sketch, "E38.0.2.9", {"start": v(-196.33, 45.36) * mm, "end": v(-198.37, 51.65) * mm});
            skLineSegment(sketch, "E38.0.3.0", {"start": v(-198.37, 13.16) * mm, "end": v(-193.02, 9.27) * mm});
            skLineSegment(sketch, "E38.0.3.1", {"start": v(-195.07, 15.56) * mm, "end": v(-189.71, 19.45) * mm});
            skLineSegment(sketch, "E38.0.3.2", {"start": v(-193.02, 9.27) * mm, "end": v(-195.07, 15.56) * mm});
            skLineSegment(sketch, "E38.0.3.3", {"start": v(-201.68, 15.56) * mm, "end": v(-203.73, 9.27) * mm});
            skLineSegment(sketch, "E38.0.3.4", {"start": v(-189.71, 19.45) * mm, "end": v(-196.33, 19.45) * mm});
            skLineSegment(sketch, "E38.0.3.5", {"start": v(-203.73, 9.27) * mm, "end": v(-198.37, 13.16) * mm});
            skLineSegment(sketch, "E38.0.3.6", {"start": v(-200.42, 19.45) * mm, "end": v(-207.03, 19.45) * mm});
            skLineSegment(sketch, "E38.0.3.7", {"start": v(-207.03, 19.45) * mm, "end": v(-201.68, 15.56) * mm});
            skLineSegment(sketch, "E38.0.3.8", {"start": v(-198.37, 25.74) * mm, "end": v(-200.42, 19.45) * mm});
            skLineSegment(sketch, "E38.0.3.9", {"start": v(-196.33, 19.45) * mm, "end": v(-198.37, 25.74) * mm});
            skLineSegment(sketch, "E38.1.0.0", {"start": v(-167.64, 90.88) * mm, "end": v(-162.29, 87) * mm});
            skLineSegment(sketch, "E38.1.0.1", {"start": v(-164.33, 93.29) * mm, "end": v(-158.98, 97.17) * mm});
            skLineSegment(sketch, "E38.1.0.2", {"start": v(-162.29, 87) * mm, "end": v(-164.33, 93.29) * mm});
            skLineSegment(sketch, "E38.1.0.3", {"start": v(-170.95, 93.29) * mm, "end": v(-173, 87) * mm});
            skLineSegment(sketch, "E38.1.0.4", {"start": v(-158.98, 97.17) * mm, "end": v(-165.6, 97.17) * mm});
            skLineSegment(sketch, "E38.1.0.5", {"start": v(-173, 87) * mm, "end": v(-167.64, 90.88) * mm});
            skLineSegment(sketch, "E38.1.0.6", {"start": v(-169.68, 97.17) * mm, "end": v(-176.3, 97.17) * mm});
            skLineSegment(sketch, "E38.1.0.7", {"start": v(-176.3, 97.17) * mm, "end": v(-170.95, 93.29) * mm});
            skLineSegment(sketch, "E38.1.0.8", {"start": v(-167.64, 103.47) * mm, "end": v(-169.68, 97.17) * mm});
            skLineSegment(sketch, "E38.1.0.9", {"start": v(-165.6, 97.17) * mm, "end": v(-167.64, 103.47) * mm});
            skLineSegment(sketch, "E38.1.1.0", {"start": v(-167.64, 64.98) * mm, "end": v(-162.29, 61.09) * mm});
            skLineSegment(sketch, "E38.1.1.1", {"start": v(-164.33, 67.38) * mm, "end": v(-158.98, 71.27) * mm});
            skLineSegment(sketch, "E38.1.1.2", {"start": v(-162.29, 61.09) * mm, "end": v(-164.33, 67.38) * mm});
            skLineSegment(sketch, "E38.1.1.3", {"start": v(-170.95, 67.38) * mm, "end": v(-173, 61.09) * mm});
            skLineSegment(sketch, "E38.1.1.4", {"start": v(-158.98, 71.27) * mm, "end": v(-165.6, 71.27) * mm});
            skLineSegment(sketch, "E38.1.1.5", {"start": v(-173, 61.09) * mm, "end": v(-167.64, 64.98) * mm});
            skLineSegment(sketch, "E38.1.1.6", {"start": v(-169.68, 71.27) * mm, "end": v(-176.3, 71.27) * mm});
            skLineSegment(sketch, "E38.1.1.7", {"start": v(-176.3, 71.27) * mm, "end": v(-170.95, 67.38) * mm});
            skLineSegment(sketch, "E38.1.1.8", {"start": v(-167.64, 77.56) * mm, "end": v(-169.68, 71.27) * mm});
            skLineSegment(sketch, "E38.1.1.9", {"start": v(-165.6, 71.27) * mm, "end": v(-167.64, 77.56) * mm});
            skLineSegment(sketch, "E38.1.2.0", {"start": v(-167.64, 39.07) * mm, "end": v(-162.29, 35.18) * mm});
            skLineSegment(sketch, "E38.1.2.1", {"start": v(-164.33, 41.47) * mm, "end": v(-158.98, 45.36) * mm});
            skLineSegment(sketch, "E38.1.2.2", {"start": v(-162.29, 35.18) * mm, "end": v(-164.33, 41.47) * mm});
            skLineSegment(sketch, "E38.1.2.3", {"start": v(-170.95, 41.47) * mm, "end": v(-173, 35.18) * mm});
            skLineSegment(sketch, "E38.1.2.4", {"start": v(-158.98, 45.36) * mm, "end": v(-165.6, 45.36) * mm});
            skLineSegment(sketch, "E38.1.2.5", {"start": v(-173, 35.18) * mm, "end": v(-167.64, 39.07) * mm});
            skLineSegment(sketch, "E38.1.2.6", {"start": v(-169.68, 45.36) * mm, "end": v(-176.3, 45.36) * mm});
            skLineSegment(sketch, "E38.1.2.7", {"start": v(-176.3, 45.36) * mm, "end": v(-170.95, 41.47) * mm});
            skLineSegment(sketch, "E38.1.2.8", {"start": v(-167.64, 51.65) * mm, "end": v(-169.68, 45.36) * mm});
            skLineSegment(sketch, "E38.1.2.9", {"start": v(-165.6, 45.36) * mm, "end": v(-167.64, 51.65) * mm});
            skLineSegment(sketch, "E38.1.3.0", {"start": v(-167.64, 13.16) * mm, "end": v(-162.29, 9.27) * mm});
            skLineSegment(sketch, "E38.1.3.1", {"start": v(-164.33, 15.56) * mm, "end": v(-158.98, 19.45) * mm});
            skLineSegment(sketch, "E38.1.3.2", {"start": v(-162.29, 9.27) * mm, "end": v(-164.33, 15.56) * mm});
            skLineSegment(sketch, "E38.1.3.3", {"start": v(-170.95, 15.56) * mm, "end": v(-173, 9.27) * mm});
            skLineSegment(sketch, "E38.1.3.4", {"start": v(-158.98, 19.45) * mm, "end": v(-165.6, 19.45) * mm});
            skLineSegment(sketch, "E38.1.3.5", {"start": v(-173, 9.27) * mm, "end": v(-167.64, 13.16) * mm});
            skLineSegment(sketch, "E38.1.3.6", {"start": v(-169.68, 19.45) * mm, "end": v(-176.3, 19.45) * mm});
            skLineSegment(sketch, "E38.1.3.7", {"start": v(-176.3, 19.45) * mm, "end": v(-170.95, 15.56) * mm});
            skLineSegment(sketch, "E38.1.3.8", {"start": v(-167.64, 25.74) * mm, "end": v(-169.68, 19.45) * mm});
            skLineSegment(sketch, "E38.1.3.9", {"start": v(-165.6, 19.45) * mm, "end": v(-167.64, 25.74) * mm});
            skLineSegment(sketch, "E38.2.0.0", {"start": v(-136.9, 90.88) * mm, "end": v(-131.55, 87) * mm});
            skLineSegment(sketch, "E38.2.0.1", {"start": v(-133.6, 93.29) * mm, "end": v(-128.25, 97.17) * mm});
            skLineSegment(sketch, "E38.2.0.2", {"start": v(-131.55, 87) * mm, "end": v(-133.6, 93.29) * mm});
            skLineSegment(sketch, "E38.2.0.3", {"start": v(-140.21, 93.29) * mm, "end": v(-142.26, 87) * mm});
            skLineSegment(sketch, "E38.2.0.4", {"start": v(-128.25, 97.17) * mm, "end": v(-134.86, 97.17) * mm});
            skLineSegment(sketch, "E38.2.0.5", {"start": v(-142.26, 87) * mm, "end": v(-136.9, 90.88) * mm});
            skLineSegment(sketch, "E38.2.0.6", {"start": v(-138.95, 97.17) * mm, "end": v(-145.57, 97.17) * mm});
            skLineSegment(sketch, "E38.2.0.7", {"start": v(-145.57, 97.17) * mm, "end": v(-140.21, 93.29) * mm});
            skLineSegment(sketch, "E38.2.0.8", {"start": v(-136.9, 103.47) * mm, "end": v(-138.95, 97.17) * mm});
            skLineSegment(sketch, "E38.2.0.9", {"start": v(-134.86, 97.17) * mm, "end": v(-136.9, 103.47) * mm});
            skLineSegment(sketch, "E38.2.1.0", {"start": v(-136.9, 64.98) * mm, "end": v(-131.55, 61.09) * mm});
            skLineSegment(sketch, "E38.2.1.1", {"start": v(-133.6, 67.38) * mm, "end": v(-128.25, 71.27) * mm});
            skLineSegment(sketch, "E38.2.1.2", {"start": v(-131.55, 61.09) * mm, "end": v(-133.6, 67.38) * mm});
            skLineSegment(sketch, "E38.2.1.3", {"start": v(-140.21, 67.38) * mm, "end": v(-142.26, 61.09) * mm});
            skLineSegment(sketch, "E38.2.1.4", {"start": v(-128.25, 71.27) * mm, "end": v(-134.86, 71.27) * mm});
            skLineSegment(sketch, "E38.2.1.5", {"start": v(-142.26, 61.09) * mm, "end": v(-136.9, 64.98) * mm});
            skLineSegment(sketch, "E38.2.1.6", {"start": v(-138.95, 71.27) * mm, "end": v(-145.57, 71.27) * mm});
            skLineSegment(sketch, "E38.2.1.7", {"start": v(-145.57, 71.27) * mm, "end": v(-140.21, 67.38) * mm});
            skLineSegment(sketch, "E38.2.1.8", {"start": v(-136.9, 77.56) * mm, "end": v(-138.95, 71.27) * mm});
            skLineSegment(sketch, "E38.2.1.9", {"start": v(-134.86, 71.27) * mm, "end": v(-136.9, 77.56) * mm});
            skLineSegment(sketch, "E38.2.2.0", {"start": v(-136.9, 39.07) * mm, "end": v(-131.55, 35.18) * mm});
            skLineSegment(sketch, "E38.2.2.1", {"start": v(-133.6, 41.47) * mm, "end": v(-128.25, 45.36) * mm});
            skLineSegment(sketch, "E38.2.2.2", {"start": v(-131.55, 35.18) * mm, "end": v(-133.6, 41.47) * mm});
            skLineSegment(sketch, "E38.2.2.3", {"start": v(-140.21, 41.47) * mm, "end": v(-142.26, 35.18) * mm});
            skLineSegment(sketch, "E38.2.2.4", {"start": v(-128.25, 45.36) * mm, "end": v(-134.86, 45.36) * mm});
            skLineSegment(sketch, "E38.2.2.5", {"start": v(-142.26, 35.18) * mm, "end": v(-136.9, 39.07) * mm});
            skLineSegment(sketch, "E38.2.2.6", {"start": v(-138.95, 45.36) * mm, "end": v(-145.57, 45.36) * mm});
            skLineSegment(sketch, "E38.2.2.7", {"start": v(-145.57, 45.36) * mm, "end": v(-140.21, 41.47) * mm});
            skLineSegment(sketch, "E38.2.2.8", {"start": v(-136.9, 51.65) * mm, "end": v(-138.95, 45.36) * mm});
            skLineSegment(sketch, "E38.2.2.9", {"start": v(-134.86, 45.36) * mm, "end": v(-136.9, 51.65) * mm});
            skLineSegment(sketch, "E38.2.3.0", {"start": v(-136.9, 13.16) * mm, "end": v(-131.55, 9.27) * mm});
            skLineSegment(sketch, "E38.2.3.1", {"start": v(-133.6, 15.56) * mm, "end": v(-128.25, 19.45) * mm});
            skLineSegment(sketch, "E38.2.3.2", {"start": v(-131.55, 9.27) * mm, "end": v(-133.6, 15.56) * mm});
            skLineSegment(sketch, "E38.2.3.3", {"start": v(-140.21, 15.56) * mm, "end": v(-142.26, 9.27) * mm});
            skLineSegment(sketch, "E38.2.3.4", {"start": v(-128.25, 19.45) * mm, "end": v(-134.86, 19.45) * mm});
            skLineSegment(sketch, "E38.2.3.5", {"start": v(-142.26, 9.27) * mm, "end": v(-136.9, 13.16) * mm});
            skLineSegment(sketch, "E38.2.3.6", {"start": v(-138.95, 19.45) * mm, "end": v(-145.57, 19.45) * mm});
            skLineSegment(sketch, "E38.2.3.7", {"start": v(-145.57, 19.45) * mm, "end": v(-140.21, 15.56) * mm});
            skLineSegment(sketch, "E38.2.3.8", {"start": v(-136.9, 25.74) * mm, "end": v(-138.95, 19.45) * mm});
            skLineSegment(sketch, "E38.2.3.9", {"start": v(-134.86, 19.45) * mm, "end": v(-136.9, 25.74) * mm});
            skLineSegment(sketch, "E38.3.0.0", {"start": v(-106.17, 90.88) * mm, "end": v(-100.82, 87) * mm});
            skLineSegment(sketch, "E38.3.0.1", {"start": v(-102.86, 93.29) * mm, "end": v(-97.51, 97.17) * mm});
            skLineSegment(sketch, "E38.3.0.2", {"start": v(-100.82, 87) * mm, "end": v(-102.86, 93.29) * mm});
            skLineSegment(sketch, "E38.3.0.3", {"start": v(-109.48, 93.29) * mm, "end": v(-111.52, 87) * mm});
            skLineSegment(sketch, "E38.3.0.4", {"start": v(-97.51, 97.17) * mm, "end": v(-104.13, 97.17) * mm});
            skLineSegment(sketch, "E38.3.0.5", {"start": v(-111.52, 87) * mm, "end": v(-106.17, 90.88) * mm});
            skLineSegment(sketch, "E38.3.0.6", {"start": v(-108.22, 97.17) * mm, "end": v(-114.83, 97.17) * mm});
            skLineSegment(sketch, "E38.3.0.7", {"start": v(-114.83, 97.17) * mm, "end": v(-109.48, 93.29) * mm});
            skLineSegment(sketch, "E38.3.0.8", {"start": v(-106.17, 103.47) * mm, "end": v(-108.22, 97.17) * mm});
            skLineSegment(sketch, "E38.3.0.9", {"start": v(-104.13, 97.17) * mm, "end": v(-106.17, 103.47) * mm});
            skLineSegment(sketch, "E38.3.1.0", {"start": v(-106.17, 64.98) * mm, "end": v(-100.82, 61.09) * mm});
            skLineSegment(sketch, "E38.3.1.1", {"start": v(-102.86, 67.38) * mm, "end": v(-97.51, 71.27) * mm});
            skLineSegment(sketch, "E38.3.1.2", {"start": v(-100.82, 61.09) * mm, "end": v(-102.86, 67.38) * mm});
            skLineSegment(sketch, "E38.3.1.3", {"start": v(-109.48, 67.38) * mm, "end": v(-111.52, 61.09) * mm});
            skLineSegment(sketch, "E38.3.1.4", {"start": v(-97.51, 71.27) * mm, "end": v(-104.13, 71.27) * mm});
            skLineSegment(sketch, "E38.3.1.5", {"start": v(-111.52, 61.09) * mm, "end": v(-106.17, 64.98) * mm});
            skLineSegment(sketch, "E38.3.1.6", {"start": v(-108.22, 71.27) * mm, "end": v(-114.83, 71.27) * mm});
            skLineSegment(sketch, "E38.3.1.7", {"start": v(-114.83, 71.27) * mm, "end": v(-109.48, 67.38) * mm});
            skLineSegment(sketch, "E38.3.1.8", {"start": v(-106.17, 77.56) * mm, "end": v(-108.22, 71.27) * mm});
            skLineSegment(sketch, "E38.3.1.9", {"start": v(-104.13, 71.27) * mm, "end": v(-106.17, 77.56) * mm});
            skLineSegment(sketch, "E38.3.2.0", {"start": v(-106.17, 39.07) * mm, "end": v(-100.82, 35.18) * mm});
            skLineSegment(sketch, "E38.3.2.1", {"start": v(-102.86, 41.47) * mm, "end": v(-97.51, 45.36) * mm});
            skLineSegment(sketch, "E38.3.2.2", {"start": v(-100.82, 35.18) * mm, "end": v(-102.86, 41.47) * mm});
            skLineSegment(sketch, "E38.3.2.3", {"start": v(-109.48, 41.47) * mm, "end": v(-111.52, 35.18) * mm});
            skLineSegment(sketch, "E38.3.2.4", {"start": v(-97.51, 45.36) * mm, "end": v(-104.13, 45.36) * mm});
            skLineSegment(sketch, "E38.3.2.5", {"start": v(-111.52, 35.18) * mm, "end": v(-106.17, 39.07) * mm});
            skLineSegment(sketch, "E38.3.2.6", {"start": v(-108.22, 45.36) * mm, "end": v(-114.83, 45.36) * mm});
            skLineSegment(sketch, "E38.3.2.7", {"start": v(-114.83, 45.36) * mm, "end": v(-109.48, 41.47) * mm});
            skLineSegment(sketch, "E38.3.2.8", {"start": v(-106.17, 51.65) * mm, "end": v(-108.22, 45.36) * mm});
            skLineSegment(sketch, "E38.3.2.9", {"start": v(-104.13, 45.36) * mm, "end": v(-106.17, 51.65) * mm});
            skLineSegment(sketch, "E38.3.3.0", {"start": v(-106.17, 13.16) * mm, "end": v(-100.82, 9.27) * mm});
            skLineSegment(sketch, "E38.3.3.1", {"start": v(-102.86, 15.56) * mm, "end": v(-97.51, 19.45) * mm});
            skLineSegment(sketch, "E38.3.3.2", {"start": v(-100.82, 9.27) * mm, "end": v(-102.86, 15.56) * mm});
            skLineSegment(sketch, "E38.3.3.3", {"start": v(-109.48, 15.56) * mm, "end": v(-111.52, 9.27) * mm});
            skLineSegment(sketch, "E38.3.3.4", {"start": v(-97.51, 19.45) * mm, "end": v(-104.13, 19.45) * mm});
            skLineSegment(sketch, "E38.3.3.5", {"start": v(-111.52, 9.27) * mm, "end": v(-106.17, 13.16) * mm});
            skLineSegment(sketch, "E38.3.3.6", {"start": v(-108.22, 19.45) * mm, "end": v(-114.83, 19.45) * mm});
            skLineSegment(sketch, "E38.3.3.7", {"start": v(-114.83, 19.45) * mm, "end": v(-109.48, 15.56) * mm});
            skLineSegment(sketch, "E38.3.3.8", {"start": v(-106.17, 25.74) * mm, "end": v(-108.22, 19.45) * mm});
            skLineSegment(sketch, "E38.3.3.9", {"start": v(-104.13, 19.45) * mm, "end": v(-106.17, 25.74) * mm});
            skLineSegment(sketch, "E38.4.0.0", {"start": v(-75.44, 90.88) * mm, "end": v(-70.09, 87) * mm});
            skLineSegment(sketch, "E38.4.0.1", {"start": v(-72.13, 93.29) * mm, "end": v(-66.78, 97.17) * mm});
            skLineSegment(sketch, "E38.4.0.2", {"start": v(-70.09, 87) * mm, "end": v(-72.13, 93.29) * mm});
            skLineSegment(sketch, "E38.4.0.3", {"start": v(-78.75, 93.29) * mm, "end": v(-80.79, 87) * mm});
            skLineSegment(sketch, "E38.4.0.4", {"start": v(-66.78, 97.17) * mm, "end": v(-73.4, 97.17) * mm});
            skLineSegment(sketch, "E38.4.0.5", {"start": v(-80.79, 87) * mm, "end": v(-75.44, 90.88) * mm});
            skLineSegment(sketch, "E38.4.0.6", {"start": v(-77.48, 97.17) * mm, "end": v(-84.1, 97.17) * mm});
            skLineSegment(sketch, "E38.4.0.7", {"start": v(-84.1, 97.17) * mm, "end": v(-78.75, 93.29) * mm});
            skLineSegment(sketch, "E38.4.0.8", {"start": v(-75.44, 103.47) * mm, "end": v(-77.48, 97.17) * mm});
            skLineSegment(sketch, "E38.4.0.9", {"start": v(-73.4, 97.17) * mm, "end": v(-75.44, 103.47) * mm});
            skLineSegment(sketch, "E38.4.1.0", {"start": v(-75.44, 64.98) * mm, "end": v(-70.09, 61.09) * mm});
            skLineSegment(sketch, "E38.4.1.1", {"start": v(-72.13, 67.38) * mm, "end": v(-66.78, 71.27) * mm});
            skLineSegment(sketch, "E38.4.1.2", {"start": v(-70.09, 61.09) * mm, "end": v(-72.13, 67.38) * mm});
            skLineSegment(sketch, "E38.4.1.3", {"start": v(-78.75, 67.38) * mm, "end": v(-80.79, 61.09) * mm});
            skLineSegment(sketch, "E38.4.1.4", {"start": v(-66.78, 71.27) * mm, "end": v(-73.4, 71.27) * mm});
            skLineSegment(sketch, "E38.4.1.5", {"start": v(-80.79, 61.09) * mm, "end": v(-75.44, 64.98) * mm});
            skLineSegment(sketch, "E38.4.1.6", {"start": v(-77.48, 71.27) * mm, "end": v(-84.1, 71.27) * mm});
            skLineSegment(sketch, "E38.4.1.7", {"start": v(-84.1, 71.27) * mm, "end": v(-78.75, 67.38) * mm});
            skLineSegment(sketch, "E38.4.1.8", {"start": v(-75.44, 77.56) * mm, "end": v(-77.48, 71.27) * mm});
            skLineSegment(sketch, "E38.4.1.9", {"start": v(-73.4, 71.27) * mm, "end": v(-75.44, 77.56) * mm});
            skLineSegment(sketch, "E38.4.2.0", {"start": v(-75.44, 39.07) * mm, "end": v(-70.09, 35.18) * mm});
            skLineSegment(sketch, "E38.4.2.1", {"start": v(-72.13, 41.47) * mm, "end": v(-66.78, 45.36) * mm});
            skLineSegment(sketch, "E38.4.2.2", {"start": v(-70.09, 35.18) * mm, "end": v(-72.13, 41.47) * mm});
            skLineSegment(sketch, "E38.4.2.3", {"start": v(-78.75, 41.47) * mm, "end": v(-80.79, 35.18) * mm});
            skLineSegment(sketch, "E38.4.2.4", {"start": v(-66.78, 45.36) * mm, "end": v(-73.4, 45.36) * mm});
            skLineSegment(sketch, "E38.4.2.5", {"start": v(-80.79, 35.18) * mm, "end": v(-75.44, 39.07) * mm});
            skLineSegment(sketch, "E38.4.2.6", {"start": v(-77.48, 45.36) * mm, "end": v(-84.1, 45.36) * mm});
            skLineSegment(sketch, "E38.4.2.7", {"start": v(-84.1, 45.36) * mm, "end": v(-78.75, 41.47) * mm});
            skLineSegment(sketch, "E38.4.2.8", {"start": v(-75.44, 51.65) * mm, "end": v(-77.48, 45.36) * mm});
            skLineSegment(sketch, "E38.4.2.9", {"start": v(-73.4, 45.36) * mm, "end": v(-75.44, 51.65) * mm});
            skLineSegment(sketch, "E38.4.3.0", {"start": v(-75.44, 13.16) * mm, "end": v(-70.09, 9.27) * mm});
            skLineSegment(sketch, "E38.4.3.1", {"start": v(-72.13, 15.56) * mm, "end": v(-66.78, 19.45) * mm});
            skLineSegment(sketch, "E38.4.3.2", {"start": v(-70.09, 9.27) * mm, "end": v(-72.13, 15.56) * mm});
            skLineSegment(sketch, "E38.4.3.3", {"start": v(-78.75, 15.56) * mm, "end": v(-80.79, 9.27) * mm});
            skLineSegment(sketch, "E38.4.3.4", {"start": v(-66.78, 19.45) * mm, "end": v(-73.4, 19.45) * mm});
            skLineSegment(sketch, "E38.4.3.5", {"start": v(-80.79, 9.27) * mm, "end": v(-75.44, 13.16) * mm});
            skLineSegment(sketch, "E38.4.3.6", {"start": v(-77.48, 19.45) * mm, "end": v(-84.1, 19.45) * mm});
            skLineSegment(sketch, "E38.4.3.7", {"start": v(-84.1, 19.45) * mm, "end": v(-78.75, 15.56) * mm});
            skLineSegment(sketch, "E38.4.3.8", {"start": v(-75.44, 25.74) * mm, "end": v(-77.48, 19.45) * mm});
            skLineSegment(sketch, "E38.4.3.9", {"start": v(-73.4, 19.45) * mm, "end": v(-75.44, 25.74) * mm});
            skLineSegment(sketch, "E38.direction1", {"start": v(-198.37, 90.88) * mm, "end": v(-167.64, 90.88) * mm, "construction": true});
            skLineSegment(sketch, "E38.direction2", {"start": v(-198.37, 90.88) * mm, "end": v(-198.37, 64.98) * mm, "construction": true});
            skSolve(sketch);
        }
        {
            var Q0;
            {var subQ7=sQuery(id+"F2.wireOp",EDGE,"E1.bottom");Q0=makeQuery(id+"F2.imprint","IMPRINT",FACE,{"disambiguationData":[TD([[makeQuery(id+"F2.imprint","IMPRINT",EDGE,{"derivedFrom":subQ7}),1.0]])]});}
            var Q1;
            Q1=makeQuery(id+"F2.imprint","IMPRINT",FACE,{"disambiguationData":[TD([[makeQuery(id+"F2.imprint","IMPRINT",EDGE,{"derivedFrom":sQuery(id+"F2.wireOp",EDGE,"E2.bottom")}),1.0]])]});
            var Q2;
            {var subQ0=sQuery(id+"F2.wireOp",EDGE,"E3.MirrorCS");Q2=makeQuery(id+"F2.imprint","IMPRINT",FACE,{"disambiguationData":[TD([[makeQuery(id+"F2.imprint","IMPRINT",EDGE,{"derivedFrom":subQ0}),-1.0]])]});}
            var Q3;
            {var subQ0=sQuery(id+"F2.wireOp",EDGE,"E5.MirrorCS");Q3=makeQuery(id+"F2.imprint","IMPRINT",FACE,{"disambiguationData":[TD([[makeQuery(id+"F2.imprint","IMPRINT",EDGE,{"derivedFrom":subQ0}),-1.0]])]});}
            var Q4;
            {var subQ2=sQuery(id+"F2.wireOp",EDGE,"E7.MirrorCS");Q4=makeQuery(id+"F2.imprint","IMPRINT",FACE,{"disambiguationData":[TD([[makeQuery(id+"F2.imprint","IMPRINT",EDGE,{"derivedFrom":subQ2}),-1.0]])]});}
            var Q5;
            {var subQ0=sQuery(id+"F2.wireOp",EDGE,"E12.MirrorCS");Q5=makeQuery(id+"F2.imprint","IMPRINT",FACE,{"disambiguationData":[TD([[makeQuery(id+"F2.imprint","IMPRINT",EDGE,{"derivedFrom":subQ0}),1.0]])]});}
            var Q6;
            {var subQ0=sQuery(id+"F2.wireOp",EDGE,"E10.MirrorCS");Q6=makeQuery(id+"F2.imprint","IMPRINT",FACE,{"disambiguationData":[TD([[makeQuery(id+"F2.imprint","IMPRINT",EDGE,{"derivedFrom":subQ0}),1.0]])]});}
            var Q7;
            Q7=makeQuery(id+"F2.imprint","IMPRINT",FACE,{"disambiguationData":[TD([[makeQuery(id+"F2.imprint","IMPRINT",EDGE,{"derivedFrom":sQuery(id+"F2.wireOp",EDGE,"E9.bottom")}),-1.0]])]});
            extrude(context, id + "F3", {"entities" : qUnion([Q0, Q1, Q2, Q3, Q4, Q5, Q6, Q7]), "operationType" : NewBodyOperationType.ADD, "depth" : 9.52 * mm});
        }
    });
